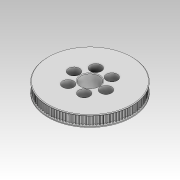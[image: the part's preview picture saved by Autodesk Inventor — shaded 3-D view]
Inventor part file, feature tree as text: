
AUTODESK INVENTOR PART (.ipt)
format: ipt  version: 2020 (Build 240168000, 168)  size: 1,109,504 bytes
history: native  units: mm
features: sketch x5, extrude x4, fillet x3, revolve x1, plane x1, pattern_circular x1, chamfer x1, projected_geometry x1
ambient origin geometry x8: Origin, YZ Plane, XZ Plane, XY Plane, X Axis, Y Axis, Z Axis, Center Point
bodies: Solid1 (feature_tree)
feature tree (17):
  revolve  "Revolution1"  [1 undecoded]
  extrude  "Extrusion1"  Depth=1.0mm
  plane  "Work Plane1"
  extrude  "Extrusion2"  Depth=33.425mm
  extrude  "Extrusion3"  TaperAngle=90.0deg  [1 undecoded]
  fillet  "Fillet1"  Radius=5.1mm
  pattern_circular  "Circular Pattern1"  Count=6 Angle=360.0deg
  fillet  "Fillet2"  [1 undecoded]
  chamfer  "Chamfer1"  [1 undecoded]
  fillet  "Fillet3"  Radius=9.0mm
  extrude  "Extrusion4"  Depth=1.0mm TaperAngle=0.0deg
  sketch  "Sketch1"  dims[d1=17.45mm d2=2.0mm]
  sketch  "Sketch2"  dims[d3=1.0mm d6=0.75mm]
  sketch  "Sketch3"  dims[d7=33.425mm d8=0.75mm]
  projected_geometry  "Projected Loop1"
  sketch  "Sketch4"  dims[d11=2.0mm d14=90.0deg d15=5.1mm]
  sketch  "Sketch5"  dims[d16=13.0mm d17=60.0mm d19=360.0deg d21=0.0mm d22=0.0mm d23=-5.0mm d24=9.0mm d25=7.0mm d26=0.0mm d27=7.5mm d29=1.0mm d30=66.85mm d31=10.0mm d32=0.0mm d33=1050.0mm d34=360.0deg d36=3.0mm d37=0.7mm d38=7.0mm d39=11.34464mm d41=34.125mm d42=0.6mm d43=0.75mm d44=0.4mm d45=0.5mm d46=0.5mm d47=2.0mm d48=45.0deg d49=1.0mm d50=0.2mm d51=0.0mm]
note: 4 required parameter values undecoded (feature->parameter linkage not recoverable at this tier; creation-order binding heuristic only, values carry confidence <= 0.55)